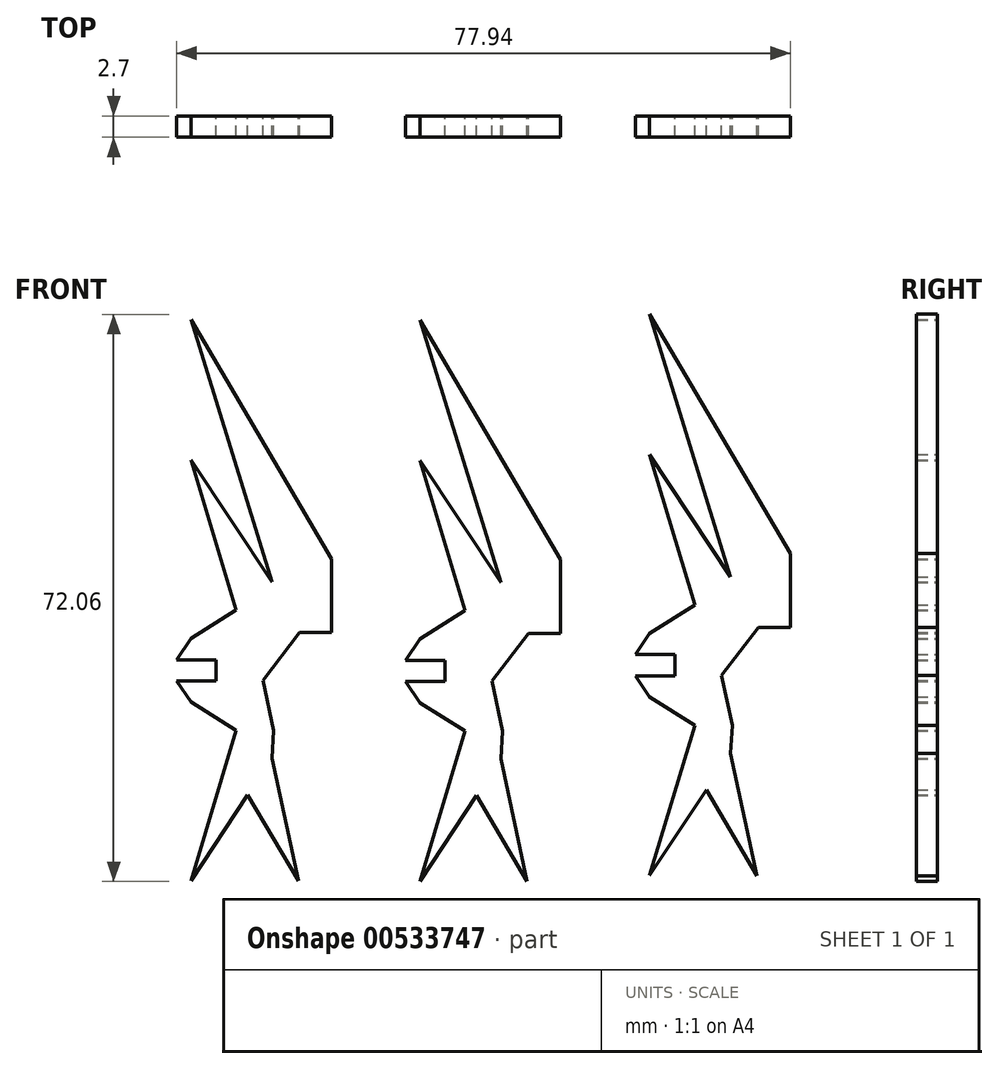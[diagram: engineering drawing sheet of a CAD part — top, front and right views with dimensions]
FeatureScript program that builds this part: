
annotation { "Feature Type Name" : "Feature", "Feature Type Description" : "" }
export const myFeature = defineFeature(function(context is Context, id is Id, definition is map)
    precondition{}
    {
        {
            var Q0;
            Q0=qCreatedBy(makeId("Front.planeOp"),FACE);
            var sketch = newSketch(context, id + "F0", { "sketchPlane" : qUnion([Q0])});
            skLineSegment(sketch, "E0", {"start": v(0, 26.73) * mm, "end": v(10.26, 11.23) * mm});
            skLineSegment(sketch, "E1.MirrorCS", {"start": v(10.26, -11.23) * mm, "end": v(10.48, -7.63) * mm});
            skLineSegment(sketch, "E2.MirrorCS", {"start": v(0, -26.73) * mm, "end": v(5.13, -18.98) * mm});
            skLineSegment(sketch, "E3", {"start": v(17.86, 14.16) * mm, "end": v(0, 44.57) * mm});
            skLineSegment(sketch, "E4", {"start": v(13.8, 4.77) * mm, "end": v(17.86, 4.77) * mm});
            skLineSegment(sketch, "E5", {"start": v(17.86, 4.77) * mm, "end": v(17.86, 14.16) * mm});
            skLineSegment(sketch, "E6", {"start": v(0, 4.06) * mm, "end": v(-1.81, 1.33) * mm});
            skLineSegment(sketch, "E7", {"start": v(-1.82, -1.37) * mm, "end": v(0, -4.06) * mm});
            skLineSegment(sketch, "E8.bottom", {"start": v(0, 1.33) * mm, "end": v(-1.81, 1.33) * mm});
            skLineSegment(sketch, "E8.top", {"start": v(0, -1.37) * mm, "end": v(-1.82, -1.37) * mm});
            skLineSegment(sketch, "E9.bottom", {"start": v(0, 1.33) * mm, "end": v(3.2, 1.33) * mm});
            skLineSegment(sketch, "E9.top", {"start": v(0, -1.37) * mm, "end": v(3.2, -1.37) * mm});
            skLineSegment(sketch, "E9.right", {"start": v(3.2, 1.33) * mm, "end": v(3.2, -1.37) * mm});
            skLineSegment(sketch, "E10", {"start": v(0, -26.73) * mm, "end": v(5.74, -7.64) * mm});
            skLineSegment(sketch, "E11", {"start": v(0, 4.06) * mm, "end": v(5.74, 7.64) * mm});
            skLineSegment(sketch, "E12", {"start": v(0, -4.06) * mm, "end": v(5.74, -7.64) * mm});
            skLineSegment(sketch, "E13", {"start": v(13.8, 4.77) * mm, "end": v(9.15, -1.29) * mm});
            skLineSegment(sketch, "E14", {"start": v(7.2, -15.85) * mm, "end": v(13.63, -26.78) * mm});
            skLineSegment(sketch, "E15", {"start": v(13.63, -26.78) * mm, "end": v(10.26, -11.23) * mm});
            skLineSegment(sketch, "E16", {"start": v(5.13, -18.98) * mm, "end": v(7.2, -15.85) * mm});
            skLineSegment(sketch, "E17", {"start": v(5.74, 7.64) * mm, "end": v(0, 26.73) * mm});
            skLineSegment(sketch, "E18", {"start": v(10.26, 11.23) * mm, "end": v(0, 44.57) * mm});
            skLineSegment(sketch, "E19", {"start": v(10.48, -7.63) * mm, "end": v(9.15, -1.29) * mm});
            skLineSegment(sketch, "E20", {"start": v(-29.08, 26.8) * mm, "end": v(-18.82, 11.3) * mm});
            skLineSegment(sketch, "E21.MirrorCS", {"start": v(-18.82, -11.16) * mm, "end": v(-18.6, -7.55) * mm});
            skLineSegment(sketch, "E22.MirrorCS", {"start": v(-29.08, -26.66) * mm, "end": v(-23.95, -18.91) * mm});
            skLineSegment(sketch, "E23", {"start": v(-11.22, 14.23) * mm, "end": v(-29.08, 44.64) * mm});
            skLineSegment(sketch, "E24", {"start": v(-15.29, 4.84) * mm, "end": v(-11.22, 4.84) * mm});
            skLineSegment(sketch, "E25", {"start": v(-11.22, 4.84) * mm, "end": v(-11.22, 14.23) * mm});
            skLineSegment(sketch, "E26", {"start": v(-29.08, 4.13) * mm, "end": v(-30.9, 1.4) * mm});
            skLineSegment(sketch, "E27", {"start": v(-30.9, -1.3) * mm, "end": v(-29.08, -3.99) * mm});
            skLineSegment(sketch, "E28.bottom", {"start": v(-29.08, 1.4) * mm, "end": v(-30.9, 1.4) * mm});
            skLineSegment(sketch, "E28.top", {"start": v(-29.08, -1.3) * mm, "end": v(-30.9, -1.3) * mm});
            skLineSegment(sketch, "E29.bottom", {"start": v(-29.08, 1.4) * mm, "end": v(-25.88, 1.4) * mm});
            skLineSegment(sketch, "E29.top", {"start": v(-29.08, -1.3) * mm, "end": v(-25.88, -1.3) * mm});
            skLineSegment(sketch, "E29.right", {"start": v(-25.88, 1.4) * mm, "end": v(-25.88, -1.3) * mm});
            skLineSegment(sketch, "E30", {"start": v(-29.08, -26.66) * mm, "end": v(-23.34, -7.57) * mm});
            skLineSegment(sketch, "E31", {"start": v(-29.08, 4.13) * mm, "end": v(-23.34, 7.7) * mm});
            skLineSegment(sketch, "E32", {"start": v(-29.08, -3.99) * mm, "end": v(-23.34, -7.57) * mm});
            skLineSegment(sketch, "E33", {"start": v(-15.29, 4.84) * mm, "end": v(-19.93, -1.22) * mm});
            skLineSegment(sketch, "E34", {"start": v(-21.87, -15.78) * mm, "end": v(-15.46, -26.7) * mm});
            skLineSegment(sketch, "E35", {"start": v(-15.46, -26.7) * mm, "end": v(-18.82, -11.16) * mm});
            skLineSegment(sketch, "E36", {"start": v(-23.95, -18.91) * mm, "end": v(-21.87, -15.78) * mm});
            skLineSegment(sketch, "E37", {"start": v(-23.34, 7.7) * mm, "end": v(-29.08, 26.8) * mm});
            skLineSegment(sketch, "E38", {"start": v(-18.82, 11.3) * mm, "end": v(-29.08, 44.64) * mm});
            skLineSegment(sketch, "E39", {"start": v(-18.6, -7.55) * mm, "end": v(-19.93, -1.22) * mm});
            skLineSegment(sketch, "E40", {"start": v(29.18, 27.44) * mm, "end": v(39.44, 11.94) * mm});
            skLineSegment(sketch, "E41.MirrorCS", {"start": v(39.44, -10.52) * mm, "end": v(39.66, -6.92) * mm});
            skLineSegment(sketch, "E42.MirrorCS", {"start": v(29.18, -26.02) * mm, "end": v(34.31, -18.27) * mm});
            skLineSegment(sketch, "E43", {"start": v(47.04, 14.87) * mm, "end": v(29.18, 45.28) * mm});
            skLineSegment(sketch, "E44", {"start": v(42.97, 5.48) * mm, "end": v(47.04, 5.48) * mm});
            skLineSegment(sketch, "E45", {"start": v(47.04, 5.48) * mm, "end": v(47.04, 14.87) * mm});
            skLineSegment(sketch, "E46", {"start": v(29.18, 4.77) * mm, "end": v(27.37, 2.04) * mm});
            skLineSegment(sketch, "E47", {"start": v(27.36, -0.66) * mm, "end": v(29.18, -3.35) * mm});
            skLineSegment(sketch, "E48.bottom", {"start": v(29.18, 2.04) * mm, "end": v(27.37, 2.04) * mm});
            skLineSegment(sketch, "E48.top", {"start": v(29.18, -0.66) * mm, "end": v(27.36, -0.66) * mm});
            skLineSegment(sketch, "E49.bottom", {"start": v(29.18, 2.04) * mm, "end": v(32.38, 2.04) * mm});
            skLineSegment(sketch, "E49.top", {"start": v(29.18, -0.66) * mm, "end": v(32.38, -0.66) * mm});
            skLineSegment(sketch, "E49.right", {"start": v(32.38, 2.04) * mm, "end": v(32.38, -0.66) * mm});
            skLineSegment(sketch, "E50", {"start": v(29.18, -26.02) * mm, "end": v(34.92, -6.93) * mm});
            skLineSegment(sketch, "E51", {"start": v(29.18, 4.77) * mm, "end": v(34.92, 8.35) * mm});
            skLineSegment(sketch, "E52", {"start": v(29.18, -3.35) * mm, "end": v(34.92, -6.93) * mm});
            skLineSegment(sketch, "E53", {"start": v(42.97, 5.48) * mm, "end": v(38.33, -0.58) * mm});
            skLineSegment(sketch, "E54", {"start": v(36.39, -15.14) * mm, "end": v(42.8, -26.07) * mm});
            skLineSegment(sketch, "E55", {"start": v(42.8, -26.07) * mm, "end": v(39.44, -10.52) * mm});
            skLineSegment(sketch, "E56", {"start": v(34.31, -18.27) * mm, "end": v(36.39, -15.14) * mm});
            skLineSegment(sketch, "E57", {"start": v(34.92, 8.35) * mm, "end": v(29.18, 27.44) * mm});
            skLineSegment(sketch, "E58", {"start": v(39.44, 11.94) * mm, "end": v(29.18, 45.28) * mm});
            skLineSegment(sketch, "E59", {"start": v(39.66, -6.92) * mm, "end": v(38.33, -0.58) * mm});
            skSolve(sketch);
        }
        {
            var Q0;
            Q0 = qSketchRegion(id + "F0", true);
            extrude(context, id + "F1", {"entities" : qUnion([Q0]), "depth" : 2.7 * mm, "offsetDistance" : 25.4 * mm});
        }
    });
